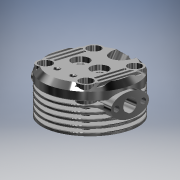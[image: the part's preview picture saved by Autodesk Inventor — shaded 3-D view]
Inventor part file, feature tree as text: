
AUTODESK INVENTOR PART (.ipt)
format: ipt  version: 2018 (Build 220112000, 112)  size: 937,472 bytes
history: native  units: mm
features: sketch x9, extrude x8, revolve x3, fillet x3, thread x3, hole x1, chamfer x1, plane x1, mirror x1
ambient origin geometry x8: Origin, YZ Plane, XZ Plane, XY Plane, X Axis, Y Axis, Z Axis, Center Point
bodies: Solid1 (feature_tree)
feature tree (30):
  revolve  "Revolution1"  [1 undecoded]
  revolve  "Revolution2"  [1 undecoded]
  extrude  "Extrusion1"  Depth=1.5mm
  sketch  "Sketch4"  dims[d6=1.5mm d7=18.0mm]
  extrude  "Extrusion2"  Depth=18.0mm
  extrude  "Extrusion3"  Depth=1.5mm
  extrude  "Extrusion4"  Depth=15.5mm
  hole  "Hole1"  [1 undecoded]
  fillet  "Fillet1"  Radius=6.0mm
  chamfer  "Chamfer1"  Angle=90.0deg  [1 undecoded]
  revolve  "Revolution3"  [1 undecoded]
  thread  "Thread1"  [1 undecoded]
  plane  "Work Plane1"
  sketch  "Sketch7"  dims[d13=2.5mm d15=11.5mm d16=6.0mm]
  extrude  "Extrusion5"  Depth=0.5mm
  extrude  "Extrusion6"  Depth=10.0mm
  extrude  "Extrusion7"  Depth=10.0mm TaperAngle=0.0deg
  thread  "Thread2"  [1 undecoded]
  thread  "Thread3"  [1 undecoded]
  extrude  "Extrusion8"  Depth=0.5mm
  mirror  "Mirror1"
  fillet  "Fillet2"  Radius=7.0mm
  fillet  "Fillet3"  Radius=4.0mm
  sketch  "Sketch1"  dims[d0=22.0mm d1=23.0mm]
  sketch  "Sketch2"  dims[d2=2.8mm d3=2.8mm]
  sketch  "Sketch3"  dims[d4=1.5mm d5=1.5mm]
  sketch  "Sketch5"  dims[d8=14.5mm d9=1.5mm]
  sketch  "Sketch6"  dims[d10=90.0deg d11=15.5mm]
  sketch  "Sketch8"  dims[d17=3.0mm]
  sketch  "Sketch9"  dims[d18=4.5mm d19=90.0deg d20=1.5mm d21=1.5mm d22=11.95mm d23=30.0mm d25=3.0mm d26=10.0mm d28=10.0mm d30=10.0mm d31=0.0mm d32=36.0mm d33=45.0deg d34=9.0mm d35=7.0mm d36=4.0mm d37=20.0mm d39=90.0deg d41=10.0mm d42=0.0mm d43=4.0mm d44=0.0mm d45=10.0mm d46=0.0mm d47=13.1mm d48=5.0mm d49=2.459mm d50=6.0mm d51=4.0mm d52=2.0mm d53=90.0deg d54=8.8mm d55=20.594885mm d56=0.5mm d57=0.5mm d58=2.0mm d59=45.0deg d60=18.0mm d61=5.585054mm d62=6.0mm d63=5.088289mm d64=3.5mm d65=12.575mm d66=90.0deg d67=10.0mm d68=0.0mm d69=7.0mm d73=10.0mm d74=6.0mm d75=12.0mm d76=10.0mm d77=2.0mm d78=0.0mm d79=0.0mm d80=10.0mm d81=0.0mm d82=3.0mm d83=7.0mm d84=10.0mm d85=0.0mm d86=10.0mm d87=0.0mm d88=10.0mm d89=0.0mm d90=9.5mm d91=6.0mm d92=12.0mm d93=6.0mm d95=3.0mm d96=0.0mm d97=0.25mm d98=0.5mm]
note: 8 required parameter values undecoded (feature->parameter linkage not recoverable at this tier; creation-order binding heuristic only, values carry confidence <= 0.55)